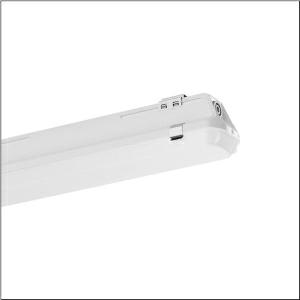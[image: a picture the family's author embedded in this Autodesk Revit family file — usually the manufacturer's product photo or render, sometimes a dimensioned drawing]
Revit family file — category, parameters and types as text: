
# Revit family: monsun_r__11_emergency_51fp107p437h3g_44d6
name_source: partatom
category: Lighting Fixtures
units: mm (PartAtom-declared; Revit-internal decimal feet)

## family parameters
Cut with Voids When Loaded = No
Host = Face
Light Source = No
Part Type = Normal
Room Calculation Point = No
Round Connector Dimension = Use Diameter
Shared = No

## types (1)
- Monsun® 11 emergency (1 x LED, 3840 lm, 24.5 W, 4000K)
    Apparent Load = 25 VA
    CIE Flux Codes = 47 77 93 94 100
    Color Rendering = 80
    Color Temperature = 4000K
    Default Elevation = 1800 mm
    Description = Monsun® 11 emergency, damp-proof luminaire, chain hanger, primary optical cover: enclosure, of PMMA, light emission: direct distribution, primary light characteristic: symmetric, installation type: suspended mounting, surface-mounted, horizontal mounting, vertical mounting, LED, rated luminous flux: 3.840lm, luminous efficacy: 157lm/W, light colour: 840, colour temperature: 4000K, control gear: ECG, with terminal, 4-pole, max. 2.5mm², mains connection: 220..240V, AC, 50/60Hz, rated input power: 25W, control gear: single battery element, battery: NiCd, 4,5Ah, mains connection: 230V, 50Hz, luminaire housing, of glass-fibre reinforced polyester, uncoated, bright grey, incl. chain hanger, length: 1.590mm, width: 90mm, height: 88mm, clip for enclosure, of stainless steel (V2A), ceiling mounting element, of stainless steel (V2A), chain hanger, of stainless steel (V2A), protection rating (complete): IP66, insulation class (complete): insulation class I (protective earthing), certification: CE, UKCA, protection symbol: D, impact resistance: IK04, permissible operating ambient temperature: +5..+35°C, standard: EN 50419, EN 60598-2-1, EN 60598-2-22, no direct snow, no direct sun, no direct rain, for indoor or canopied outdoor use, corresponds to IFS (International Featured Standards) requirements for safety and quality in the food industry, contact your sales advisor before using the luminaires in applications with unclear chemical exposure, large temperature fluctuations or condensation-forming humidity, LABS conformity tested according to VDMA 24364:2018-05, packaging unit: 1 piece
    Height = 89 mm
    Lamp = 1 x LED
    Lamp Light Flux = 3840 lm
    Lamp Power = 24.5 W
    Lamp count = 1
    Length = 1590 mm
    Luminous efficacy = 157 lm/W
    Manufacturer = Siteco
    ModVariant = No
    Model = 51FP107P437H3G
    Mounting Place = Ceiling
    Mounting Type = Surface mounted
    Number of Poles = 1
    OnlyDefault = Yes
    Power Factor = 1
    Product Name = Monsun® 11 emergency
    Product group = damp-proof luminaire
    ProductGroupID = 301
    Protection Class = Protection class I
    Protection Degree = IP 66
    RLX_Detail_Level = 1
    RLX_Emergency_Light_Flux = 0 lm
    RLX_Emergency_Type = 0
    RLX_Emergency_Type_DB = No
    RlxData = <blob elided: 88961 chars, md5=cf5b19e5>
    Socket = socket
    Standby Power = 0 W
    System Light Flux = 3840 lm
    System Power = 25 W
    Type Comments = Product without accessories
    Type Image = l_1004748.jpg
    URL = http://relux.com
    VarID = ---
    Voltage = 0 V
    Weight = 0.00 kg
    Width = 90 mm

## geometry (parser evidence)
native form markers: Blend x4, Sweep x14
no freeform markers — native parametric forms only
